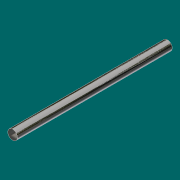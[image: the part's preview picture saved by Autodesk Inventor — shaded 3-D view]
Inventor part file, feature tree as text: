
AUTODESK INVENTOR PART (.ipt)
format: ipt  version: 2017 (Build 210142000, 142)  size: 71,680 bytes
history: native  units: in
note: dims shown in document units (in); Inventor stores cm internally (conversion verified against a paired STEP export)
features: extrude x1, sketch x1
ambient origin geometry x8: Origin, YZ Plane, XZ Plane, XY Plane, X Axis, Y Axis, Z Axis, Center Point
bodies: Solid1 (feature_tree)
feature tree (2):
  extrude  "Extrusion1"  Depth=36.0in TaperAngle=0.0deg
  sketch  "Sketch1"  dims[d0=2.25in d1=36.0in d2=0.0in]
